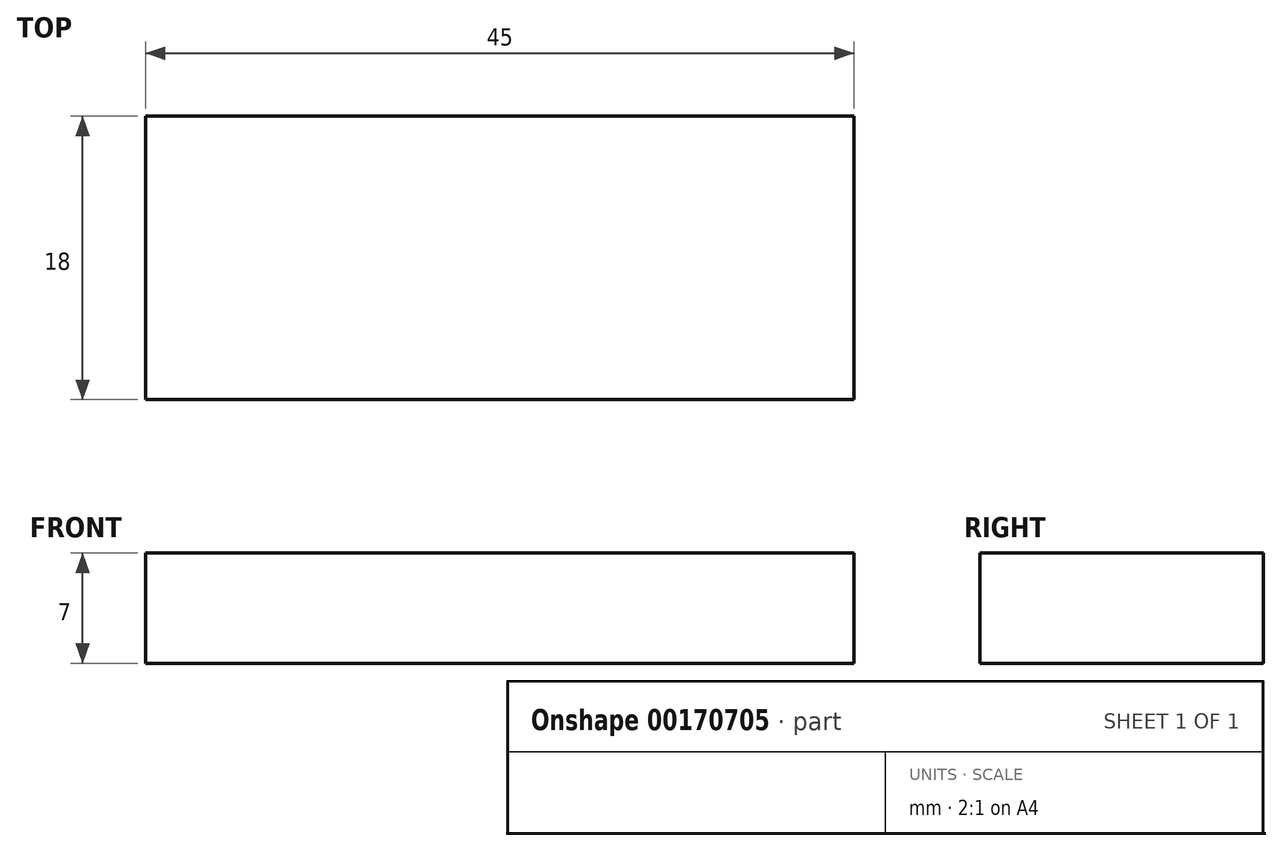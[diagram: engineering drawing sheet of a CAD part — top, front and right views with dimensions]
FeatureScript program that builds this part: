
annotation { "Feature Type Name" : "Feature", "Feature Type Description" : "" }
export const myFeature = defineFeature(function(context is Context, id is Id, definition is map)
    precondition{}
    {
        {
            var Q0;
            Q0=qCreatedBy(makeId("Top.planeOp"),FACE);
            var sketch = newSketch(context, id + "F0", { "sketchPlane" : qUnion([Q0])});
            skLineSegment(sketch, "E0.bottom", {"start": v(0, 0) * mm, "end": v(45, 0) * mm});
            skLineSegment(sketch, "E0.top", {"start": v(0, 18) * mm, "end": v(45, 18) * mm});
            skLineSegment(sketch, "E0.left", {"start": v(0, 0) * mm, "end": v(0, 18) * mm});
            skLineSegment(sketch, "E0.right", {"start": v(45, 0) * mm, "end": v(45, 18) * mm});
            skSolve(sketch);
        }
        {
            var Q0;
            Q0=makeQuery(id+"F0.imprint","IMPRINT",FACE,{"disambiguationData":[TD([[makeQuery(id+"F0.imprint","IMPRINT",EDGE,{"derivedFrom":sQuery(id+"F0.wireOp",EDGE,"E0.bottom")}),1.0]])]});
            extrude(context, id + "F1", {"entities" : qUnion([Q0]), "depth" : 7 * mm});
        }
    });
